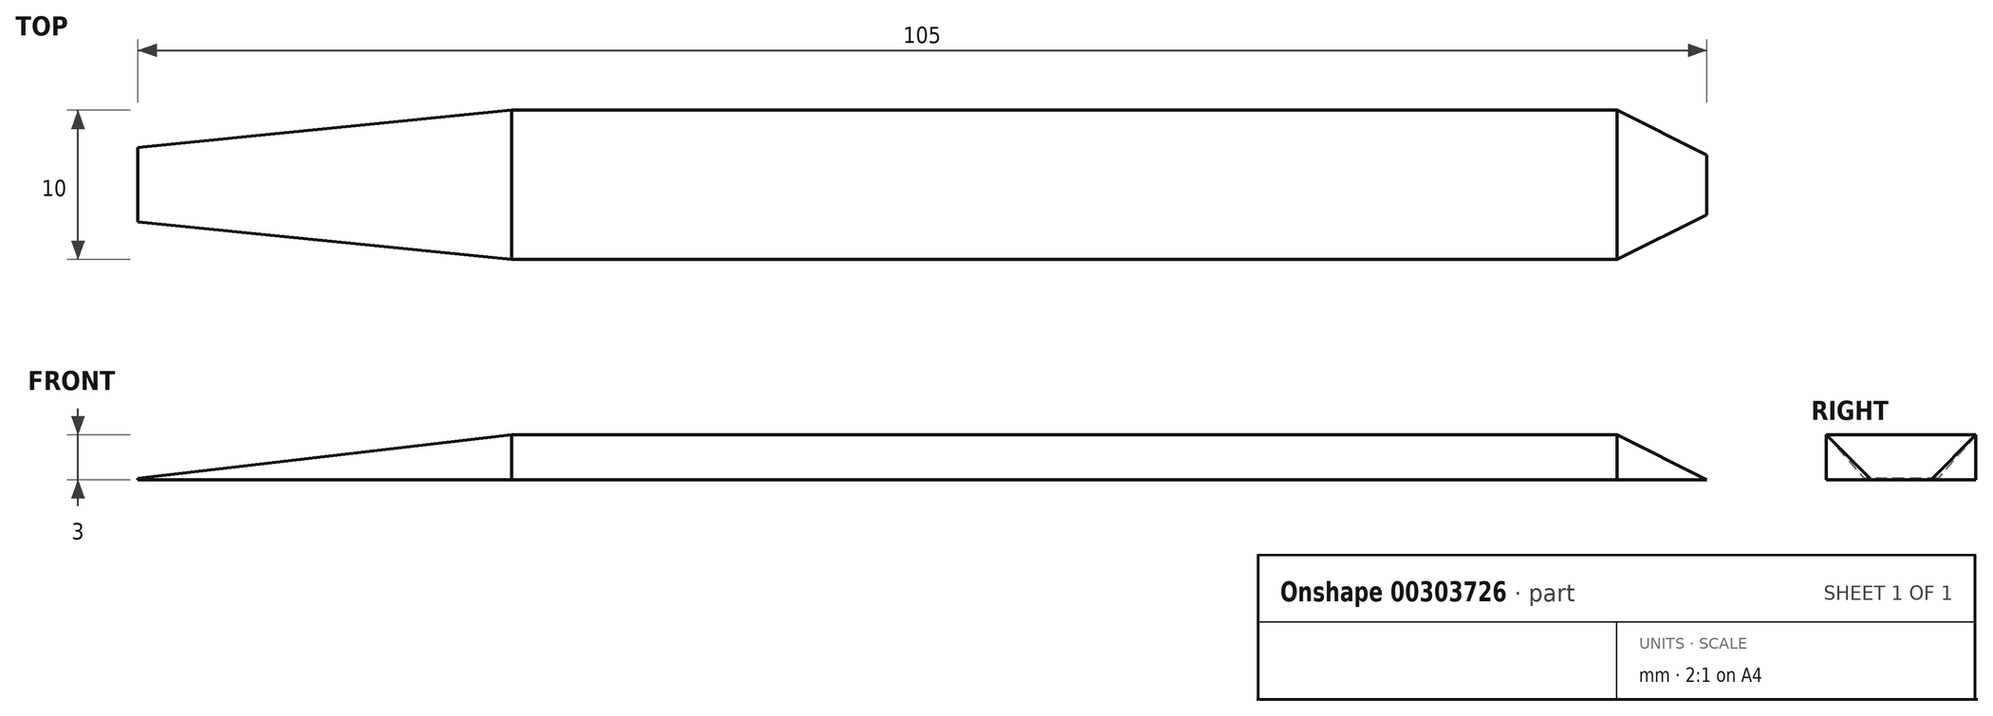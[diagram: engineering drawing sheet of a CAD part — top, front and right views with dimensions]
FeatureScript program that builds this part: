
annotation { "Feature Type Name" : "Feature", "Feature Type Description" : "" }
export const myFeature = defineFeature(function(context is Context, id is Id, definition is map)
    precondition{}
    {
        {
            var Q0;
            Q0=qCreatedBy(makeId("Top.planeOp"),FACE);
            var sketch = newSketch(context, id + "F0", { "sketchPlane" : qUnion([Q0])});
            skLineSegment(sketch, "E0.bottom", {"start": v(-40, 0) * mm, "end": v(40, 0) * mm});
            skLineSegment(sketch, "E0.top", {"start": v(-40, 10) * mm, "end": v(40, 10) * mm});
            skLineSegment(sketch, "E0.left", {"start": v(-40, 0) * mm, "end": v(-40, 10) * mm});
            skLineSegment(sketch, "E0.right", {"start": v(40, 0) * mm, "end": v(40, 10) * mm});
            skLineSegment(sketch, "E1", {"start": v(-40, 0) * mm, "end": v(-65, 2.5) * mm});
            skLineSegment(sketch, "E2", {"start": v(-65, 2.5) * mm, "end": v(-65, 7.5) * mm});
            skLineSegment(sketch, "E3", {"start": v(-65, 7.5) * mm, "end": v(-40, 10) * mm});
            skLineSegment(sketch, "E4", {"start": v(-40, 5) * mm, "end": v(-78.4, 5) * mm, "construction": true});
            skSolve(sketch);
        }
        {
            var Q0;
            Q0=makeQuery(id+"F0.imprint","IMPRINT",FACE,{"disambiguationData":[TD([[makeQuery(id+"F0.imprint","IMPRINT",EDGE,{"derivedFrom":sQuery(id+"F0.wireOp",EDGE,"E0.bottom")}),1.0]])]});
            extrude(context, id + "F1", {"entities" : qUnion([Q0]), "depth" : 3 * mm});
        }
        {
            var Q0;
            Q0=qCreatedBy(makeId("Right.planeOp"),FACE);
            var Q1;
            Q1=sQuery(id+"F0.wireOp",VERTEX,"E2.start");
            cPlane(context, id + "F2", {"entities" : qUnion([Q0, Q1]), "cplaneType" : CPlaneType.PLANE_POINT, "offset" : 25 * mm, "width" : 150 * mm, "height" : 150 * mm});
        }
        {
            var Q0;
            Q0=qCreatedBy(id+"F2.planeOp",FACE);
            var sketch = newSketch(context, id + "F3", { "sketchPlane" : qUnion([Q0])});
            skLineSegment(sketch, "E5.0", {"start": v(2.5, 0) * mm, "end": v(7.5, 0) * mm});
            skLineSegment(sketch, "E6", {"start": v(7.5, 0) * mm, "end": v(7.5, 0.1) * mm});
            skLineSegment(sketch, "E7", {"start": v(7.5, 0.1) * mm, "end": v(2.5, 0.1) * mm});
            skLineSegment(sketch, "E8", {"start": v(2.5, 0.1) * mm, "end": v(2.5, 0) * mm});
            skSolve(sketch);
        }
        {
            var Q1;
            Q1=makeQuery(id+"F1.opExtrude","SWEPT_FACE",FACE,{"disambiguationData":[OSD([sQuery(id+"F0.wireOp",EDGE,"E0.left")])]});
            var Q2;
            Q2 = qSketchRegion(id + "F3", true);
            loft(context, id + "F4", {"operationType" : NewBodyOperationType.ADD, "sheetProfilesArray" : [{ "sheetProfileEntities" : qUnion([Q1]) }, { "sheetProfileEntities" : qUnion([Q2]) }]});
        }
        {
            var Q0;
            Q0=makeQuery(id+"F1.opExtrude","CAP_EDGE",EDGE,{"disambiguationData":[OSD([sQuery(id+"F0.wireOp",EDGE,"E0.right")])],"isStart":false});
            var Q1;
            Q1=makeQuery(id+"F1.opExtrude","SWEPT_EDGE",EDGE,{"disambiguationData":[OSD([sQuery(id+"F0.wireOp",EDGE,"E0.bottom"),sQuery(id+"F0.wireOp",EDGE,"E0.right")])]});
            var Q2;
            Q2=makeQuery(id+"F1.opExtrude","SWEPT_EDGE",EDGE,{"disambiguationData":[OSD([sQuery(id+"F0.wireOp",EDGE,"E0.top"),sQuery(id+"F0.wireOp",EDGE,"E0.right")])]});
            chamfer(context, id + "F5", {"entities" : qUnion([Q0, Q1, Q2]), "chamferType" : ChamferType.TWO_OFFSETS, "width1" : 6 * mm, "oppositeDirection" : false, "width2" : 3 * mm, "tangentPropagation" : true});
        }
    });
